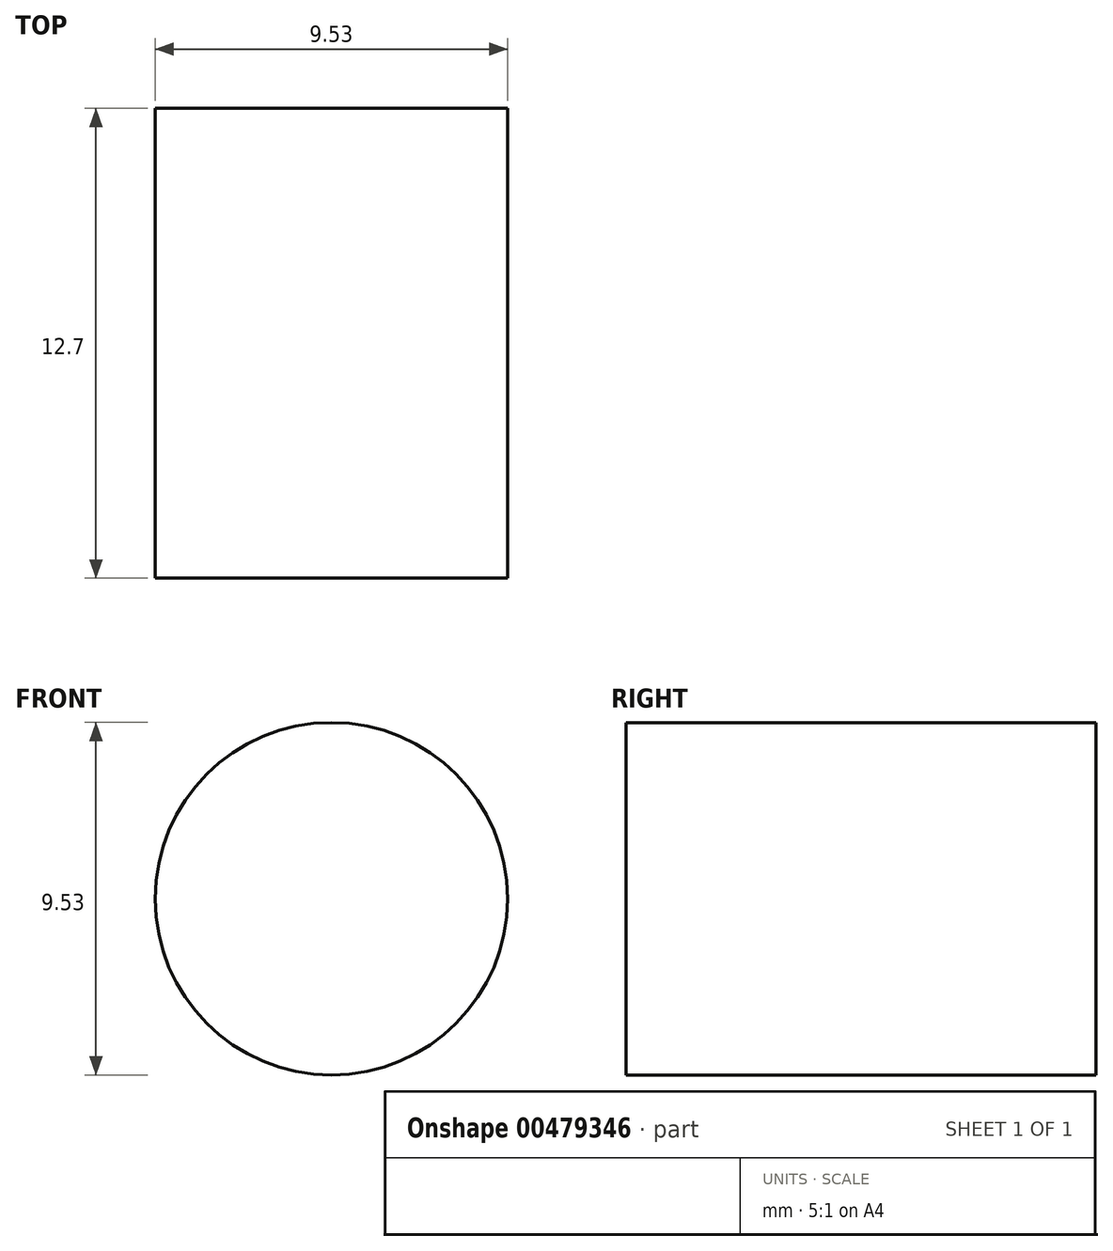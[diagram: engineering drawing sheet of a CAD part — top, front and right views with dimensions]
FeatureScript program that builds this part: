
annotation { "Feature Type Name" : "Feature", "Feature Type Description" : "" }
export const myFeature = defineFeature(function(context is Context, id is Id, definition is map)
    precondition{}
    {
        {
            var Q0;
            Q0=qCreatedBy(makeId("Front.planeOp"),FACE);
            var sketch = newSketch(context, id + "F0", { "sketchPlane" : qUnion([Q0])});
            skCircle(sketch, "E0", {"center": v(-20.23, 11.25) * mm, "radius": 4.76 * mm});
            skSolve(sketch);
        }
        {
            var Q0;
            Q0=makeQuery(id+"F0.imprint","IMPRINT",FACE,{"disambiguationData":[TD([[makeQuery(id+"F0.imprint","IMPRINT",EDGE,{"derivedFrom":sQuery(id+"F0.wireOp",EDGE,"E0")}),1.0]])]});
            extrude(context, id + "F1", {"entities" : qUnion([Q0]), "depth" : 12.7 * mm});
        }
    });
